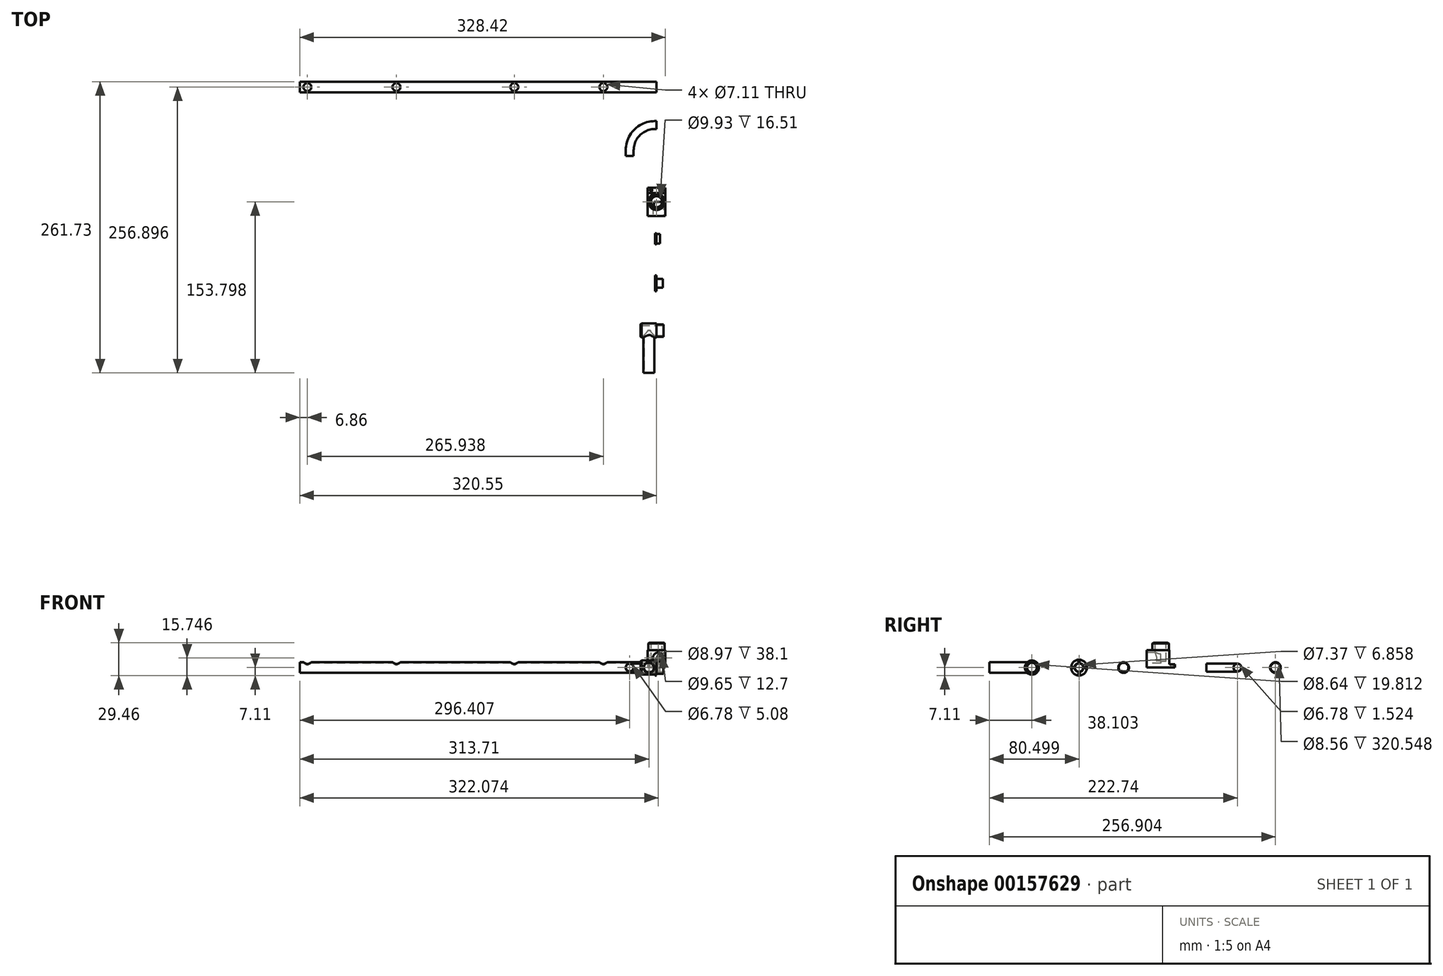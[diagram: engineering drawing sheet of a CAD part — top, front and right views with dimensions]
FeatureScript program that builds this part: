
annotation { "Feature Type Name" : "Feature", "Feature Type Description" : "" }
export const myFeature = defineFeature(function(context is Context, id is Id, definition is map)
    precondition{}
    {
        {
            var Q0;
            Q0=qCreatedBy(makeId("Top.planeOp"),FACE);
            var sketch = newSketch(context, id + "F0", { "sketchPlane" : qUnion([Q0])});
            skLineSegment(sketch, "E0", {"start": v(0, 0) * mm, "end": v(-1.52, 0) * mm, "construction": true});
            skLineSegment(sketch, "E1", {"start": v(-24.14, -22.62) * mm, "end": v(-24.14, -27.7) * mm, "construction": true});
            skArc(sketch, "E2", {"start": v(-1.52, 0) * mm, "mid": v(-17.52, -6.62) * mm, "end": v(-24.14, -22.62) * mm});
            skLineSegment(sketch, "E3", {"start": v(-24.14, -22.62) * mm, "end": v(-24.14, -27.7) * mm});
            skLineSegment(sketch, "E4", {"start": v(0, 0) * mm, "end": v(-1.52, 0) * mm});
            skSolve(sketch);
        }
        {
            var Q0;
            Q0=qCreatedBy(makeId("Right.planeOp"),FACE);
            var sketch = newSketch(context, id + "F1", { "sketchPlane" : qUnion([Q0])});
            skCircle(sketch, "E5", {"center": v(0, 0) * mm, "radius": 3.57 * mm});
            skSolve(sketch);
        }
        {
            var Q0;
            Q0=makeQuery(id+"F1.imprint","IMPRINT",FACE,{"disambiguationData":[TD([[makeQuery(id+"F1.imprint","IMPRINT",EDGE,{"derivedFrom":sQuery(id+"F1.wireOp",EDGE,"E5")}),1.0]])]});
            var Q1;
            Q1=sQuery(id+"F0.wireOp",EDGE,"E4");
            var Q2;
            Q2=sQuery(id+"F0.wireOp",EDGE,"E2");
            var Q3;
            Q3=sQuery(id+"F0.wireOp",EDGE,"E3");
            sweep(context, id + "F2", {"profiles" : qUnion([Q0]), "path" : qUnion([Q1, Q2, Q3])});
        }
        {
            var Q0;
            Q0=makeQuery(id+"F2.opSweep","CAP_FACE",FACE,{"disambiguationData":[OSD([sQuery(id+"F0.wireOp",VERTEX,"E4.start"),sQuery(id+"F1.wireOp",EDGE,"E5")])],"isStart":true});
            var sketch = newSketch(context, id + "F3", { "sketchPlane" : qUnion([Q0])});
            skCircle(sketch, "E6", {"center": v(0, 0) * mm, "radius": 3.4 * mm});
            skSolve(sketch);
        }
        {
            var Q0;
            Q0=makeQuery(id+"F3.imprint","IMPRINT",FACE,{"disambiguationData":[TD([[makeQuery(id+"F3.imprint","IMPRINT",EDGE,{"derivedFrom":sQuery(id+"F3.wireOp",EDGE,"E6")}),1.0]])]});
            var Q1;
            Q1 = qConstructionFilter(qBodyType(qCreatedBy(id + "F0" ,EDGE), BodyType.WIRE), ConstructionObject.NO);
            sweep(context, id + "F4", {"operationType" : NewBodyOperationType.REMOVE, "profiles" : qUnion([Q0]), "path" : qUnion([Q1])});
        }
        {
            var Q0;
            Q0=qCreatedBy(makeId("Right.planeOp"),FACE);
            var sketch = newSketch(context, id + "F5", { "sketchPlane" : qUnion([Q0])});
            skCircle(sketch, "E7", {"center": v(34.16, 0) * mm, "radius": 4.83 * mm});
            skSolve(sketch);
        }
        {
            var Q0;
            Q0=makeQuery(id+"F5.imprint","IMPRINT",FACE,{"disambiguationData":[TD([[makeQuery(id+"F5.imprint","IMPRINT",EDGE,{"derivedFrom":sQuery(id+"F5.wireOp",EDGE,"E7")}),1.0]])]});
            extrude(context, id + "F6", {"entities" : qUnion([Q0]), "oppositeDirection" : true, "depth" : 320.55 * mm});
        }
        {
            var Q0;
            Q0=makeQuery(id+"F6.opExtrude","CAP_FACE",FACE,{"disambiguationData":[OSD([sQuery(id+"F5.wireOp",EDGE,"E7")])],"isStart":true});
            var sketch = newSketch(context, id + "F7", { "sketchPlane" : qUnion([Q0])});
            skCircle(sketch, "E8", {"center": v(34.16, 0) * mm, "radius": 4.28 * mm});
            skSolve(sketch);
        }
        {
            var Q0;
            Q0=makeQuery(id+"F7.imprint","IMPRINT",FACE,{"disambiguationData":[TD([[makeQuery(id+"F7.imprint","IMPRINT",EDGE,{"derivedFrom":sQuery(id+"F7.wireOp",EDGE,"E8")}),1.0]])]});
            extrude(context, id + "F8", {"entities" : qUnion([Q0]), "operationType" : NewBodyOperationType.REMOVE, "endBound" : BoundingType.THROUGH_ALL, "oppositeDirection" : true, "depth" : 25.4 * mm});
        }
        {
            var Q0;
            Q0=makeQuery(id+"F6.opExtrude","CAP_FACE",FACE,{"disambiguationData":[OSD([sQuery(id+"F5.wireOp",EDGE,"E7")])],"isStart":true});
            var sketch = newSketch(context, id + "F9", { "sketchPlane" : qUnion([Q0])});
            skLineSegment(sketch, "E9", {"start": v(34.16, 0) * mm, "end": v(34.16, 4.83) * mm});
            skSolve(sketch);
        }
        {
            var Q0;
            Q0=qCreatedBy(makeId("Top.planeOp"),FACE);
            var Q1;
            Q1=sQuery(id+"F9.wireOp",VERTEX,"E9.end");
            cPlane(context, id + "F10", {"entities" : qUnion([Q0, Q1]), "cplaneType" : CPlaneType.PLANE_POINT, "offset" : 25.4 * mm, "width" : 152.4 * mm, "height" : 152.4 * mm});
        }
        {
            var Q0;
            Q0=qCreatedBy(id+"F10.planeOp",FACE);
            var sketch = newSketch(context, id + "F11", { "sketchPlane" : qUnion([Q0])});
            skLineSegment(sketch, "E10", {"start": v(0, 34.16) * mm, "end": v(-456.63, 34.16) * mm, "construction": true});
            skCircle(sketch, "E11", {"center": v(-47.75, 34.16) * mm, "radius": 3.56 * mm});
            skCircle(sketch, "E12", {"center": v(-127.76, 34.16) * mm, "radius": 3.56 * mm});
            skCircle(sketch, "E13", {"center": v(-233.68, 34.16) * mm, "radius": 3.56 * mm});
            skCircle(sketch, "E14", {"center": v(-313.7, 34.16) * mm, "radius": 3.56 * mm});
            skSolve(sketch);
        }
        {
            var Q0;
            Q0=makeQuery(id+"F11.imprint","IMPRINT",FACE,{"disambiguationData":[TD([[makeQuery(id+"F11.imprint","IMPRINT",EDGE,{"derivedFrom":sQuery(id+"F11.wireOp",EDGE,"E14")}),1.0]])]});
            var Q1;
            Q1=makeQuery(id+"F11.imprint","IMPRINT",FACE,{"disambiguationData":[TD([[makeQuery(id+"F11.imprint","IMPRINT",EDGE,{"derivedFrom":sQuery(id+"F11.wireOp",EDGE,"E13")}),1.0]])]});
            var Q2;
            Q2=makeQuery(id+"F11.imprint","IMPRINT",FACE,{"disambiguationData":[TD([[makeQuery(id+"F11.imprint","IMPRINT",EDGE,{"derivedFrom":sQuery(id+"F11.wireOp",EDGE,"E12")}),1.0]])]});
            var Q3;
            Q3=makeQuery(id+"F11.imprint","IMPRINT",FACE,{"disambiguationData":[TD([[makeQuery(id+"F11.imprint","IMPRINT",EDGE,{"derivedFrom":sQuery(id+"F11.wireOp",EDGE,"E11")}),1.0]])]});
            extrude(context, id + "F12", {"entities" : qUnion([Q0, Q1, Q2, Q3]), "operationType" : NewBodyOperationType.REMOVE, "oppositeDirection" : true, "depth" : 5.08 * mm});
        }
        {
            var Q0;
            Q0=qCreatedBy(makeId("Top.planeOp"),FACE);
            var sketch = newSketch(context, id + "F13", { "sketchPlane" : qUnion([Q0])});
            skLineSegment(sketch, "E15.bottom", {"start": v(-7.87, -56.24) * mm, "end": v(7.87, -56.24) * mm});
            skLineSegment(sketch, "E15.top", {"start": v(-7.87, -81.64) * mm, "end": v(7.87, -81.64) * mm});
            skLineSegment(sketch, "E15.left", {"start": v(-7.87, -56.24) * mm, "end": v(-7.87, -81.64) * mm});
            skLineSegment(sketch, "E15.right", {"start": v(7.87, -56.24) * mm, "end": v(7.87, -81.64) * mm});
            skPoint(sketch, "E15.middle", {"position": v(0, -68.94) * mm});
            skLineSegment(sketch, "E16", {"start": v(7.87, -61.07) * mm, "end": v(-7.87, -61.07) * mm});
            skSolve(sketch);
        }
        {
            var Q0;
            {var subQ0=sQuery(id+"F13.wireOp",EDGE,"E15.top");Q0=makeQuery(id+"F13.imprint","IMPRINT",FACE,{"disambiguationData":[TD([[makeQuery(id+"F13.imprint","IMPRINT",EDGE,{"derivedFrom":subQ0}),1.0]])]});}
            extrude(context, id + "F14", {"entities" : qUnion([Q0]), "depth" : 15.75 * mm});
        }
        {
            var Q0;
            {var subQ0=sQuery(id+"F13.wireOp",EDGE,"E15.bottom");Q0=makeQuery(id+"F13.imprint","IMPRINT",FACE,{"disambiguationData":[TD([[makeQuery(id+"F13.imprint","IMPRINT",EDGE,{"derivedFrom":subQ0}),-1.0]])]});}
            extrude(context, id + "F15", {"entities" : qUnion([Q0]), "operationType" : NewBodyOperationType.ADD, "depth" : 3.05 * mm});
        }
        {
            var Q0;
            Q0=makeQuery(id+"F14.opExtrude","CAP_FACE",FACE,{"disambiguationData":[OSD([sQuery(id+"F13.wireOp",EDGE,"E15.top"),sQuery(id+"F13.wireOp",EDGE,"E15.left"),sQuery(id+"F13.wireOp",EDGE,"E15.right"),sQuery(id+"F13.wireOp",EDGE,"E16")])],"isStart":false});
            var sketch = newSketch(context, id + "F16", { "sketchPlane" : qUnion([Q0])});
            skCircle(sketch, "E17", {"center": v(0, -68.94) * mm, "radius": 7.37 * mm});
            skPoint(sketch, "E17.centerSnap0", {"position": v(0, -61.07) * mm});
            skSolve(sketch);
        }
        {
            var Q0;
            Q0=makeQuery(id+"F16.imprint","IMPRINT",FACE,{"disambiguationData":[TD([[makeQuery(id+"F16.imprint","IMPRINT",EDGE,{"derivedFrom":sQuery(id+"F16.wireOp",EDGE,"E17")}),1.0]])]});
            extrude(context, id + "F17", {"entities" : qUnion([Q0]), "operationType" : NewBodyOperationType.ADD, "depth" : 6.6 * mm});
        }
        {
            var Q0;
            Q0=makeQuery(id+"F17.opExtrude","CAP_EDGE",EDGE,{"disambiguationData":[OSD([sQuery(id+"F16.wireOp",EDGE,"E17")])],"isStart":false});
            chamfer(context, id + "F18", {"entities" : qUnion([Q0]), "width" : 0.76 * mm, "tangentPropagation" : true});
        }
        {
            var Q0;
            Q0=makeQuery(id+"F15.opExtrude","CAP_FACE",FACE,{"disambiguationData":[OSD([sQuery(id+"F13.wireOp",EDGE,"E15.bottom"),sQuery(id+"F13.wireOp",EDGE,"E15.left"),sQuery(id+"F13.wireOp",EDGE,"E15.right"),sQuery(id+"F13.wireOp",EDGE,"E16")])],"isStart":false});
            var sketch = newSketch(context, id + "F19", { "sketchPlane" : qUnion([Q0])});
            skCircle(sketch, "E18", {"center": v(4.83, -58.66) * mm, "radius": 1.1 * mm});
            skPoint(sketch, "E18.centerSnap0", {"position": v(7.87, -58.66) * mm});
            skCircle(sketch, "E19", {"center": v(-4.83, -58.66) * mm, "radius": 1.1 * mm});
            skSolve(sketch);
        }
        {
            var Q0;
            Q0=makeQuery(id+"F19.imprint","IMPRINT",FACE,{"disambiguationData":[TD([[makeQuery(id+"F19.imprint","IMPRINT",EDGE,{"derivedFrom":sQuery(id+"F19.wireOp",EDGE,"E19")}),1.0]])]});
            var Q1;
            Q1=makeQuery(id+"F19.imprint","IMPRINT",FACE,{"disambiguationData":[TD([[makeQuery(id+"F19.imprint","IMPRINT",EDGE,{"derivedFrom":sQuery(id+"F19.wireOp",EDGE,"E18")}),1.0]])]});
            extrude(context, id + "F20", {"entities" : qUnion([Q0, Q1]), "operationType" : NewBodyOperationType.REMOVE, "oppositeDirection" : true, "depth" : 25.4 * mm});
        }
        {
            var Q0;
            Q0=makeQuery(id+"F17.opExtrude","CAP_FACE",FACE,{"disambiguationData":[OSD([sQuery(id+"F16.wireOp",EDGE,"E17")])],"isStart":false});
            var sketch = newSketch(context, id + "F21", { "sketchPlane" : qUnion([Q0])});
            skCircle(sketch, "E20", {"center": v(0, -68.94) * mm, "radius": 4.97 * mm});
            skSolve(sketch);
        }
        {
            var Q0;
            Q0=makeQuery(id+"F21.imprint","IMPRINT",FACE,{"disambiguationData":[TD([[makeQuery(id+"F21.imprint","IMPRINT",EDGE,{"derivedFrom":sQuery(id+"F21.wireOp",EDGE,"E20")}),1.0]])]});
            extrude(context, id + "F22", {"entities" : qUnion([Q0]), "operationType" : NewBodyOperationType.REMOVE, "oppositeDirection" : true, "depth" : 16.5 * mm});
        }
        {
            var Q0;
            Q0=makeQuery(id+"F14.opExtrude","SWEPT_FACE",FACE,{"disambiguationData":[OSD([sQuery(id+"F13.wireOp",EDGE,"E15.top")])]});
            var sketch = newSketch(context, id + "F23", { "sketchPlane" : qUnion([Q0])});
            skCircle(sketch, "E21", {"center": v(1.52, 8.64) * mm, "radius": 4.83 * mm});
            skSolve(sketch);
        }
        {
            var Q0;
            Q0=makeQuery(id+"F23.imprint","IMPRINT",FACE,{"disambiguationData":[TD([[makeQuery(id+"F23.imprint","IMPRINT",EDGE,{"derivedFrom":sQuery(id+"F23.wireOp",EDGE,"E21")}),1.0]])]});
            extrude(context, id + "F24", {"entities" : qUnion([Q0]), "operationType" : NewBodyOperationType.REMOVE, "oppositeDirection" : true, "depth" : 12.7 * mm});
        }
        {
            var Q0;
            Q0=qCreatedBy(makeId("Right.planeOp"),FACE);
            var sketch = newSketch(context, id + "F25", { "sketchPlane" : qUnion([Q0])});
            skCircle(sketch, "E22", {"center": v(-102.24, 0) * mm, "radius": 4.83 * mm});
            skSolve(sketch);
        }
        {
            var Q0;
            Q0=makeQuery(id+"F25.imprint","IMPRINT",FACE,{"disambiguationData":[TD([[makeQuery(id+"F25.imprint","IMPRINT",EDGE,{"derivedFrom":sQuery(id+"F25.wireOp",EDGE,"E22")}),1.0]])]});
            extrude(context, id + "F26", {"entities" : qUnion([Q0]), "oppositeDirection" : true, "depth" : 1.27 * mm});
        }
        {
            var Q0;
            Q0=makeQuery(id+"F26.opExtrude","CAP_FACE",FACE,{"disambiguationData":[OSD([sQuery(id+"F25.wireOp",EDGE,"E22")])],"isStart":true});
            var sketch = newSketch(context, id + "F27", { "sketchPlane" : qUnion([Q0])});
            skCircle(sketch, "E23", {"center": v(-102.24, 0) * mm, "radius": 4.32 * mm});
            skSolve(sketch);
        }
        {
            var Q0;
            Q0=makeQuery(id+"F27.imprint","IMPRINT",FACE,{"disambiguationData":[TD([[makeQuery(id+"F27.imprint","IMPRINT",EDGE,{"derivedFrom":sQuery(id+"F27.wireOp",EDGE,"E23")}),1.0]])]});
            extrude(context, id + "F28", {"entities" : qUnion([Q0]), "operationType" : NewBodyOperationType.ADD, "depth" : 3.05 * mm});
        }
        {
            var Q0;
            Q0=qCreatedBy(makeId("Right.planeOp"),FACE);
            var sketch = newSketch(context, id + "F29", { "sketchPlane" : qUnion([Q0])});
            skCircle(sketch, "E24", {"center": v(-142.24, 0) * mm, "radius": 7.11 * mm});
            skCircle(sketch, "E25", {"center": v(-142.24, 0) * mm, "radius": 4.06 * mm});
            skCircle(sketch, "E26", {"center": v(-142.24, 0) * mm, "radius": 3.68 * mm});
            skSolve(sketch);
        }
        {
            var Q0;
            Q0=makeQuery(id+"F29.imprint","IMPRINT",FACE,{"disambiguationData":[TD([[makeQuery(id+"F29.imprint","IMPRINT",EDGE,{"derivedFrom":sQuery(id+"F29.wireOp",EDGE,"E24")}),1.0]])]});
            var Q1;
            Q1=makeQuery(id+"F29.imprint","IMPRINT",FACE,{"disambiguationData":[TD([[makeQuery(id+"F29.imprint","IMPRINT",EDGE,{"derivedFrom":sQuery(id+"F29.wireOp",EDGE,"E25")}),1.0]])]});
            extrude(context, id + "F30", {"entities" : qUnion([Q0, Q1]), "oppositeDirection" : true, "depth" : 1.27 * mm});
        }
        {
            var Q0;
            Q0=makeQuery(id+"F29.imprint","IMPRINT",FACE,{"disambiguationData":[TD([[makeQuery(id+"F29.imprint","IMPRINT",EDGE,{"derivedFrom":sQuery(id+"F29.wireOp",EDGE,"E25")}),1.0]])]});
            extrude(context, id + "F31", {"entities" : qUnion([Q0]), "operationType" : NewBodyOperationType.ADD, "depth" : 5.6 * mm});
        }
        {
            var Q0;
            Q0=makeQuery(id+"F30.opExtrude","CAP_FACE",FACE,{"disambiguationData":[OSD([sQuery(id+"F29.wireOp",EDGE,"E24"),sQuery(id+"F29.wireOp",EDGE,"E26")])],"isStart":false});
            var sketch = newSketch(context, id + "F32", { "sketchPlane" : qUnion([Q0])});
            skCircle(sketch, "E27", {"center": v(142.24, 0) * mm, "radius": 5.84 * mm, "construction": true});
            skCircle(sketch, "E28", {"center": v(136.4, 0) * mm, "radius": 0.76 * mm});
            skCircle(sketch, "E29", {"center": v(148.08, 0) * mm, "radius": 0.76 * mm});
            skCircle(sketch, "E30", {"center": v(142.24, 5.84) * mm, "radius": 0.76 * mm});
            skCircle(sketch, "E31", {"center": v(142.24, -5.84) * mm, "radius": 0.76 * mm});
            skSolve(sketch);
        }
        {
            var Q0;
            Q0=makeQuery(id+"F32.imprint","IMPRINT",FACE,{"disambiguationData":[TD([[makeQuery(id+"F32.imprint","IMPRINT",EDGE,{"derivedFrom":sQuery(id+"F32.wireOp",EDGE,"E28")}),1.0]])]});
            var Q1;
            Q1=makeQuery(id+"F32.imprint","IMPRINT",FACE,{"disambiguationData":[TD([[makeQuery(id+"F32.imprint","IMPRINT",EDGE,{"derivedFrom":sQuery(id+"F32.wireOp",EDGE,"E30")}),1.0]])]});
            var Q2;
            Q2=makeQuery(id+"F32.imprint","IMPRINT",FACE,{"disambiguationData":[TD([[makeQuery(id+"F32.imprint","IMPRINT",EDGE,{"derivedFrom":sQuery(id+"F32.wireOp",EDGE,"E29")}),1.0]])]});
            var Q3;
            Q3=makeQuery(id+"F32.imprint","IMPRINT",FACE,{"disambiguationData":[TD([[makeQuery(id+"F32.imprint","IMPRINT",EDGE,{"derivedFrom":sQuery(id+"F32.wireOp",EDGE,"E31")}),1.0]])]});
            extrude(context, id + "F33", {"entities" : qUnion([Q0, Q1, Q2, Q3]), "operationType" : NewBodyOperationType.REMOVE, "oppositeDirection" : true, "depth" : 25.4 * mm});
        }
        {
            var Q0;
            Q0=qCreatedBy(makeId("Right.planeOp"),FACE);
            var sketch = newSketch(context, id + "F34", { "sketchPlane" : qUnion([Q0])});
            skCircle(sketch, "E32", {"center": v(-184.64, 0) * mm, "radius": 6.35 * mm});
            skCircle(sketch, "E33", {"center": v(-184.64, 0) * mm, "radius": 5.56 * mm});
            skCircle(sketch, "E34", {"center": v(-184.64, 0) * mm, "radius": 4.32 * mm});
            skSolve(sketch);
        }
        {
            var Q0;
            Q0=makeQuery(id+"F34.imprint","IMPRINT",FACE,{"disambiguationData":[TD([[makeQuery(id+"F34.imprint","IMPRINT",EDGE,{"derivedFrom":sQuery(id+"F34.wireOp",EDGE,"E32")}),1.0]])]});
            var Q1;
            Q1=makeQuery(id+"F34.imprint","IMPRINT",FACE,{"disambiguationData":[TD([[makeQuery(id+"F34.imprint","IMPRINT",EDGE,{"derivedFrom":sQuery(id+"F34.wireOp",EDGE,"E33")}),1.0]])]});
            var Q2;
            Q2=makeQuery(id+"F34.imprint","IMPRINT",FACE,{"disambiguationData":[TD([[makeQuery(id+"F34.imprint","IMPRINT",EDGE,{"derivedFrom":sQuery(id+"F34.wireOp",EDGE,"E34")}),1.0]])]});
            extrude(context, id + "F35", {"entities" : qUnion([Q0, Q1, Q2]), "oppositeDirection" : true, "depth" : 14.22 * mm});
        }
        {
            var Q0;
            Q0=makeQuery(id+"F34.imprint","IMPRINT",FACE,{"disambiguationData":[TD([[makeQuery(id+"F34.imprint","IMPRINT",EDGE,{"derivedFrom":sQuery(id+"F34.wireOp",EDGE,"E33")}),1.0]])]});
            var Q1;
            Q1=makeQuery(id+"F34.imprint","IMPRINT",FACE,{"disambiguationData":[TD([[makeQuery(id+"F34.imprint","IMPRINT",EDGE,{"derivedFrom":sQuery(id+"F34.wireOp",EDGE,"E34")}),1.0]])]});
            extrude(context, id + "F36", {"entities" : qUnion([Q0, Q1]), "operationType" : NewBodyOperationType.ADD, "depth" : 6.35 * mm});
        }
        {
            var Q0;
            Q0=makeQuery(id+"F36.opExtrude","CAP_FACE",FACE,{"disambiguationData":[OSD([sQuery(id+"F34.wireOp",EDGE,"E33")])],"isStart":false});
            var sketch = newSketch(context, id + "F37", { "sketchPlane" : qUnion([Q0])});
            skCircle(sketch, "E35", {"center": v(-184.64, 0) * mm, "radius": 4.32 * mm});
            skSolve(sketch);
        }
        {
            var Q0;
            Q0=makeQuery(id+"F35.opExtrude","CAP_FACE",FACE,{"disambiguationData":[OSD([sQuery(id+"F34.wireOp",EDGE,"E32")])],"isStart":false});
            var sketch = newSketch(context, id + "F38", { "sketchPlane" : qUnion([Q0])});
            skLineSegment(sketch, "E36", {"start": v(184.64, 0) * mm, "end": v(190.99, 0) * mm});
            skSolve(sketch);
        }
        {
            var Q0;
            Q0=sQuery(id+"F38.wireOp",VERTEX,"E36.end");
            var Q1;
            Q1=qCreatedBy(makeId("Front.planeOp"),FACE);
            cPlane(context, id + "F39", {"entities" : qUnion([Q0, Q1]), "cplaneType" : CPlaneType.PLANE_POINT, "offset" : 25.4 * mm, "width" : 152.4 * mm, "height" : 152.4 * mm});
        }
        {
            var Q0;
            Q0=qCreatedBy(id+"F39.planeOp",FACE);
            var sketch = newSketch(context, id + "F40", { "sketchPlane" : qUnion([Q0])});
            skCircle(sketch, "E37", {"center": v(-6.84, 0) * mm, "radius": 4.83 * mm});
            skSolve(sketch);
        }
        {
            var Q0;
            Q0=makeQuery(id+"F40.imprint","IMPRINT",FACE,{"disambiguationData":[TD([[makeQuery(id+"F40.imprint","IMPRINT",EDGE,{"derivedFrom":sQuery(id+"F40.wireOp",EDGE,"E37")}),1.0]])]});
            extrude(context, id + "F41", {"entities" : qUnion([Q0]), "operationType" : NewBodyOperationType.ADD, "oppositeDirection" : true, "depth" : 6.35 * mm, "hasSecondDirection" : true, "secondDirectionOppositeDirection" : false, "secondDirectionDepth" : 31.75 * mm});
        }
        {
            var Q0;
            Q0=makeQuery(id+"F41.opExtrude","CAP_FACE",FACE,{"disambiguationData":[OSD([sQuery(id+"F40.wireOp",EDGE,"E37")])],"isStart":true});
            var sketch = newSketch(context, id + "F42", { "sketchPlane" : qUnion([Q0])});
            skCircle(sketch, "E38", {"center": v(-6.84, 0) * mm, "radius": 4.49 * mm});
            skSolve(sketch);
        }
        {
            var Q0;
            Q0=makeQuery(id+"F42.imprint","IMPRINT",FACE,{"disambiguationData":[TD([[makeQuery(id+"F42.imprint","IMPRINT",EDGE,{"derivedFrom":sQuery(id+"F42.wireOp",EDGE,"E38")}),1.0]])]});
            extrude(context, id + "F43", {"entities" : qUnion([Q0]), "operationType" : NewBodyOperationType.REMOVE, "oppositeDirection" : true, "depth" : 38.1 * mm});
        }
        {
            var Q0;
            Q0=makeQuery(id+"F37.imprint","IMPRINT",FACE,{"disambiguationData":[TD([[makeQuery(id+"F37.imprint","IMPRINT",EDGE,{"derivedFrom":sQuery(id+"F37.wireOp",EDGE,"E35")}),1.0]])]});
            extrude(context, id + "F44", {"entities" : qUnion([Q0]), "operationType" : NewBodyOperationType.REMOVE, "oppositeDirection" : true, "depth" : 19.8 * mm});
        }
        {
            var Q0;
            Q0=makeQuery(id+"F35.opExtrude","CAP_EDGE",EDGE,{"disambiguationData":[OSD([sQuery(id+"F34.wireOp",EDGE,"E32")])],"isStart":false});
            chamfer(context, id + "F45", {"entities" : qUnion([Q0]), "width" : 0.76 * mm, "tangentPropagation" : true});
        }
    });
